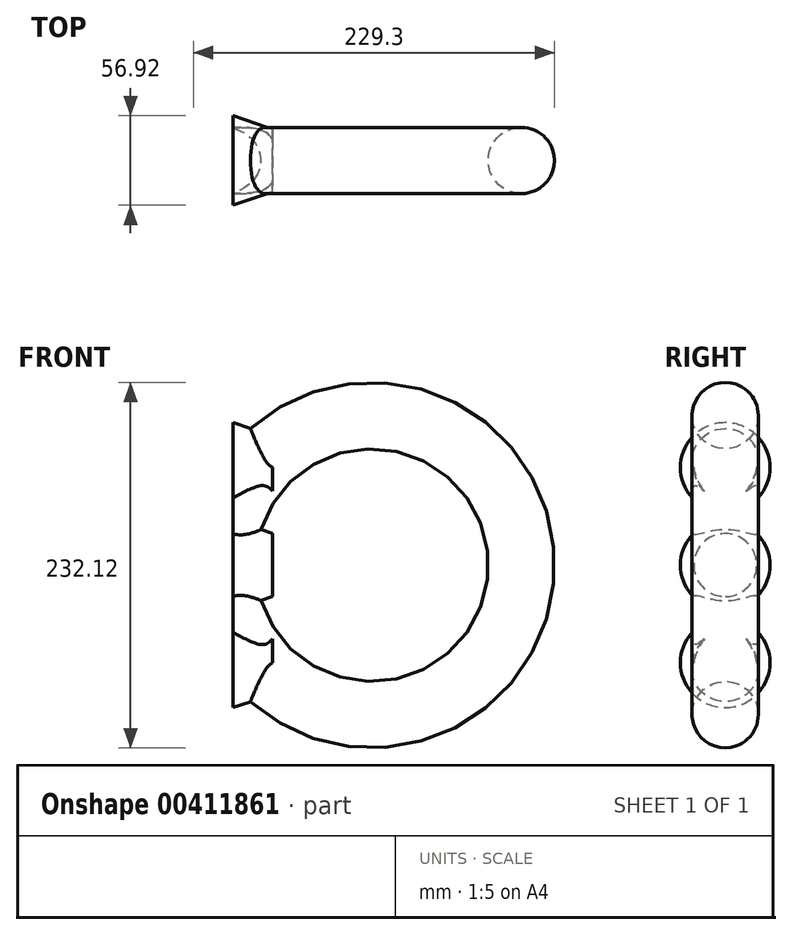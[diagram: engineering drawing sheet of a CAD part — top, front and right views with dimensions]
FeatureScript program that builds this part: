
annotation { "Feature Type Name" : "Feature", "Feature Type Description" : "" }
export const myFeature = defineFeature(function(context is Context, id is Id, definition is map)
    precondition{}
    {
        {
            var Q0;
            Q0=qCreatedBy(makeId("Front.planeOp"),FACE);
            var sketch = newSketch(context, id + "F0", { "sketchPlane" : qUnion([Q0])});
            skLineSegment(sketch, "E0.bottom", {"start": v(-95, 95) * mm, "end": v(95, 95) * mm});
            skLineSegment(sketch, "E0.top", {"start": v(-95, -95) * mm, "end": v(95, -95) * mm});
            skLineSegment(sketch, "E0.left", {"start": v(-95, 95) * mm, "end": v(-95, -95) * mm});
            skLineSegment(sketch, "E0.right", {"start": v(95, 95) * mm, "end": v(95, -95) * mm});
            skPoint(sketch, "E0.middle", {"position": v(0, 0) * mm});
            skCircle(sketch, "E1", {"center": v(0, 0) * mm, "radius": 95 * mm});
            skFitSpline(sketch, "E2", {"points": [v(0, 95) * mm, v(64.3, 69.94) * mm, v(71.64, -62.39) * mm, v(-54.05, -78.13) * mm, v(0, 95) * mm]});
            skSolve(sketch);
        }
        {
            var Q0;
            Q0=qCreatedBy(makeId("Top.planeOp"),FACE);
            var sketch = newSketch(context, id + "F1", { "sketchPlane" : qUnion([Q0])});
            skLineSegment(sketch, "E3", {"start": v(0, 0) * mm, "end": v(0, -89.87) * mm});
            skSolve(sketch);
        }
        {
            var Q0;
            Q0=qCreatedBy(makeId("Right.planeOp"),FACE);
            var sketch = newSketch(context, id + "F2", { "sketchPlane" : qUnion([Q0])});
            skPoint(sketch, "E4.0", {"position": v(0, 95) * mm});
            skCircle(sketch, "E5", {"center": v(0, 95) * mm, "radius": 21.06 * mm});
            skLineSegment(sketch, "E6.0", {"start": v(0, -97.23) * mm, "end": v(0, 101.7) * mm});
            skSolve(sketch);
        }
        {
            var Q0;
            Q0=makeQuery(id+"F2.imprint","IMPRINT",FACE,{"disambiguationData":[TD([[makeQuery(id+"F2.imprint","IMPRINT",EDGE,{"derivedFrom":sQuery(id+"F2.wireOp",EDGE,"E5")}),1.0]])]});
            var Q1;
            Q1=sQuery(id+"F0.wireOp",EDGE,"E1");
            revolve(context, id + "F3", {"entities" : qUnion([Q0]), "axis" : qUnion([Q1]), "revolveType" : RevolveType.FULL});
        }
        {
            var Q0;
            Q0=qCreatedBy(makeId("Right.planeOp"),FACE);
            cPlane(context, id + "F4", {"entities" : qUnion([Q0]), "cplaneType" : CPlaneType.OFFSET, "offset" : 88 * mm, "oppositeDirection" : true, "width" : 150 * mm, "height" : 150 * mm});
        }
        {
            var Q0;
            Q0=qCreatedBy(id+"F4.planeOp",FACE);
            var sketch = newSketch(context, id + "F5", { "sketchPlane" : qUnion([Q0])});
            skCircle(sketch, "E7", {"center": v(0, 0) * mm, "radius": 28.46 * mm});
            skCircle(sketch, "E8.0.1.0", {"center": v(0, 62) * mm, "radius": 28.46 * mm});
            skLineSegment(sketch, "E8.direction1", {"start": v(0, 0) * mm, "end": v(25, 0) * mm, "construction": true});
            skLineSegment(sketch, "E8.direction2", {"start": v(0, 0) * mm, "end": v(0, 62) * mm, "construction": true});
            skCircle(sketch, "E9.0.1.0", {"center": v(0, -62) * mm, "radius": 28.46 * mm});
            skLineSegment(sketch, "E9.direction2", {"start": v(0, 0) * mm, "end": v(0, -62) * mm, "construction": true});
            skSolve(sketch);
        }
        {
            var Q0;
            Q0=qCreatedBy(id+"F4.planeOp",FACE);
            cPlane(context, id + "F6", {"entities" : qUnion([Q0]), "cplaneType" : CPlaneType.OFFSET, "offset" : 25 * mm, "width" : 150 * mm, "height" : 150 * mm});
        }
        {
            var Q0;
            Q0=qCreatedBy(id+"F6.planeOp",FACE);
            var sketch = newSketch(context, id + "F7", { "sketchPlane" : qUnion([Q0])});
            skCircle(sketch, "E10", {"center": v(0, 0) * mm, "radius": 20 * mm});
            skCircle(sketch, "E11.0.1.0", {"center": v(0, 62) * mm, "radius": 20 * mm});
            skLineSegment(sketch, "E11.direction1", {"start": v(0, 0) * mm, "end": v(308.84, 0) * mm, "construction": true});
            skLineSegment(sketch, "E11.direction2", {"start": v(0, 0) * mm, "end": v(0, 62) * mm, "construction": true});
            skCircle(sketch, "E12.0.1.0", {"center": v(0, -62) * mm, "radius": 20 * mm});
            skLineSegment(sketch, "E12.direction1", {"start": v(0, 0) * mm, "end": v(25, 0) * mm, "construction": true});
            skLineSegment(sketch, "E12.direction2", {"start": v(0, 0) * mm, "end": v(0, -62) * mm, "construction": true});
            skSolve(sketch);
        }
        {
            var Q1;
            Q1=makeQuery(id+"F5.imprint","IMPRINT",FACE,{"disambiguationData":[TD([[makeQuery(id+"F5.imprint","IMPRINT",EDGE,{"derivedFrom":sQuery(id+"F5.wireOp",EDGE,"E8.0.1.0")}),1.0]])]});
            var Q2;
            Q2=makeQuery(id+"F7.imprint","IMPRINT",FACE,{"disambiguationData":[TD([[makeQuery(id+"F7.imprint","IMPRINT",EDGE,{"derivedFrom":sQuery(id+"F7.wireOp",EDGE,"E11.0.1.0")}),1.0]])]});
            loft(context, id + "F8", {"operationType" : NewBodyOperationType.ADD, "sheetProfilesArray" : [{ "sheetProfileEntities" : qUnion([Q1]) }, { "sheetProfileEntities" : qUnion([Q2]) }]});
        }
        {
            var Q0;
            Q0=qCreatedBy(id+"F4.planeOp",FACE);
            var sketch = newSketch(context, id + "F9", { "sketchPlane" : qUnion([Q0])});
            skLineSegment(sketch, "E13.bottom", {"start": v(138.11, 153.97) * mm, "end": v(-146.63, 153.97) * mm});
            skLineSegment(sketch, "E13.top", {"start": v(138.11, -150.48) * mm, "end": v(-146.63, -150.48) * mm});
            skLineSegment(sketch, "E13.left", {"start": v(138.11, 153.97) * mm, "end": v(138.11, -150.48) * mm});
            skLineSegment(sketch, "E13.right", {"start": v(-146.63, 153.97) * mm, "end": v(-146.63, -150.48) * mm});
            skSolve(sketch);
        }
        {
            var Q0;
            Q0 = qSketchRegion(id + "F9", true);
            extrude(context, id + "F10", {"entities" : qUnion([Q0]), "operationType" : NewBodyOperationType.REMOVE, "oppositeDirection" : true, "depth" : 160 * mm});
        }
        {
            var Q1;
            Q1=makeQuery(id+"F5.imprint","IMPRINT",FACE,{"disambiguationData":[TD([[makeQuery(id+"F5.imprint","IMPRINT",EDGE,{"derivedFrom":sQuery(id+"F5.wireOp",EDGE,"E9.0.1.0")}),1.0]])]});
            var Q2;
            Q2=makeQuery(id+"F7.imprint","IMPRINT",FACE,{"disambiguationData":[TD([[makeQuery(id+"F7.imprint","IMPRINT",EDGE,{"derivedFrom":sQuery(id+"F7.wireOp",EDGE,"E12.0.1.0")}),1.0]])]});
            loft(context, id + "F11", {"operationType" : NewBodyOperationType.ADD, "sheetProfilesArray" : [{ "sheetProfileEntities" : qUnion([Q1]) }, { "sheetProfileEntities" : qUnion([Q2]) }]});
        }
        {
            var Q1;
            Q1=makeQuery(id+"F5.imprint","IMPRINT",FACE,{"disambiguationData":[TD([[makeQuery(id+"F5.imprint","IMPRINT",EDGE,{"derivedFrom":sQuery(id+"F5.wireOp",EDGE,"E7")}),1.0]])]});
            var Q2;
            Q2=makeQuery(id+"F7.imprint","IMPRINT",FACE,{"disambiguationData":[TD([[makeQuery(id+"F7.imprint","IMPRINT",EDGE,{"derivedFrom":sQuery(id+"F7.wireOp",EDGE,"E10")}),1.0]])]});
            loft(context, id + "F12", {"operationType" : NewBodyOperationType.ADD, "sheetProfilesArray" : [{ "sheetProfileEntities" : qUnion([Q1]) }, { "sheetProfileEntities" : qUnion([Q2]) }]});
        }
    });
